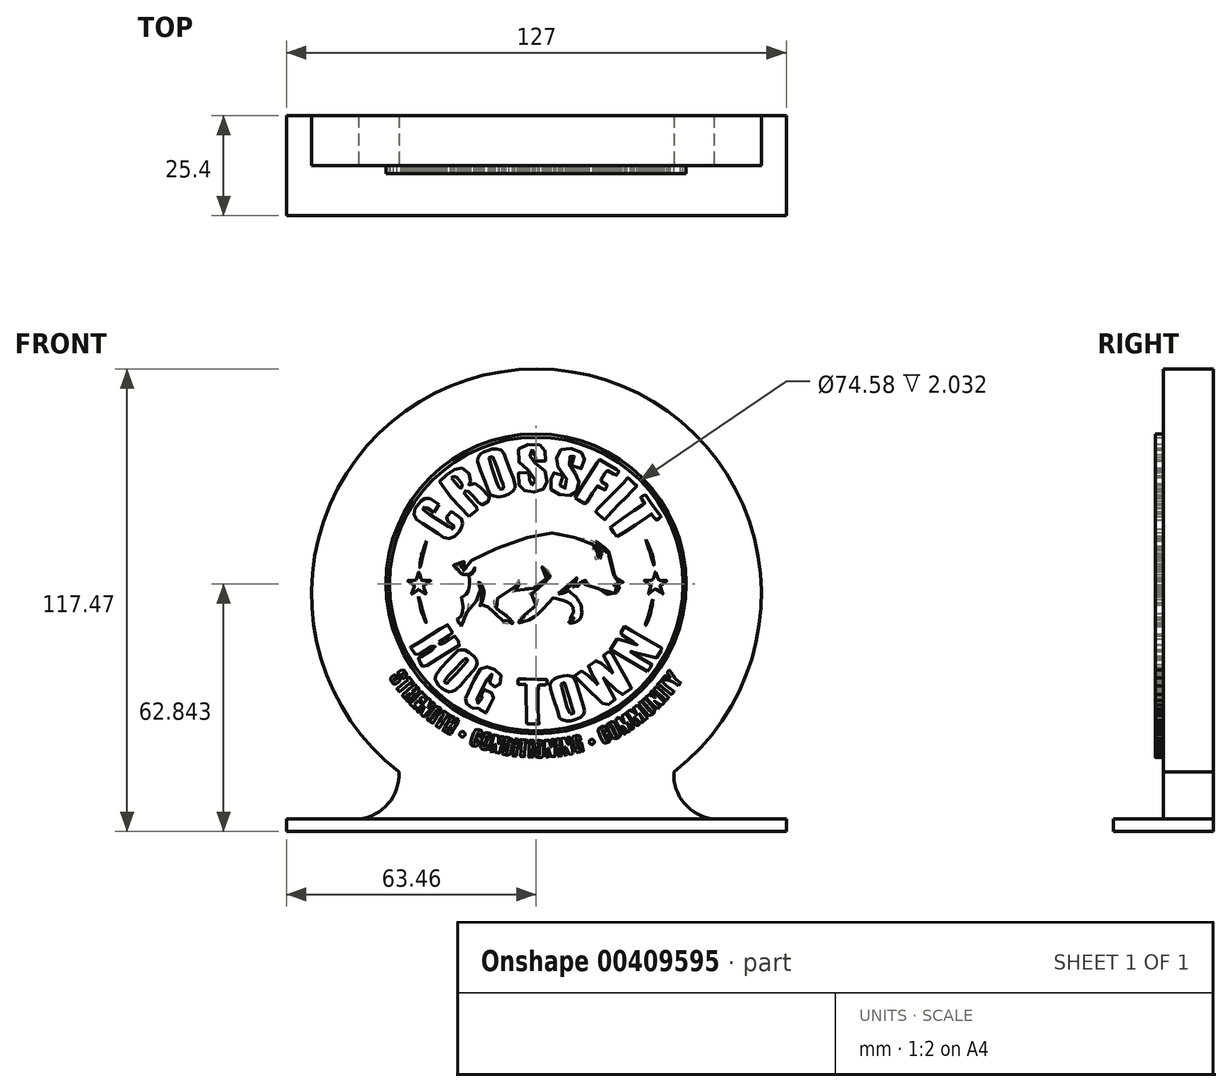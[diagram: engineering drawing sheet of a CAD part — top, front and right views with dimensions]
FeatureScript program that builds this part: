
annotation { "Feature Type Name" : "Feature", "Feature Type Description" : "" }
export const myFeature = defineFeature(function(context is Context, id is Id, definition is map)
    precondition{}
    {
        {
            var Q0;
            Q0=qCreatedBy(makeId("Front.planeOp"),FACE);
            var sketch = newSketch(context, id + "F0", { "sketchPlane" : qUnion([Q0])});
            skCircle(sketch, "E0", {"center": v(0, 0) * mm, "radius": 57.15 * mm});
            skSolve(sketch);
        }
        {
            var Q0;
            Q0=makeQuery(id+"F0.imprint","IMPRINT",FACE,{"disambiguationData":[TD([[makeQuery(id+"F0.imprint","IMPRINT",EDGE,{"derivedFrom":sQuery(id+"F0.wireOp",EDGE,"E0")}),1.0]])]});
            var Q1;
            Q1 = qSketchRegion(id + "F2", true);
            extrude(context, id + "F1", {"entities" : qUnion([Q0, Q1]), "endBound" : BoundingType.SYMMETRIC, "depth" : 12.7 * mm});
        }
        {
            var Q0;
            Q0=makeQuery(id+"F1.opExtrude","CAP_FACE",FACE,{"disambiguationData":[OSD([sQuery(id+"F0.wireOp",EDGE,"E0")])],"isStart":false});
            var sketch = newSketch(context, id + "F2", { "sketchPlane" : qUnion([Q0])});
            skLineSegment(sketch, "E1", {"start": v(-26.03, 20.73) * mm, "end": v(-24.68, 22.7) * mm});
            skLineSegment(sketch, "E2", {"start": v(-24.68, 22.7) * mm, "end": v(-27.02, 24.31) * mm});
            skLineSegment(sketch, "E3", {"start": v(-27.02, 24.31) * mm, "end": v(-28.26, 24.31) * mm});
            skLineSegment(sketch, "E4", {"start": v(-28.26, 24.31) * mm, "end": v(-29.26, 23.65) * mm});
            skLineSegment(sketch, "E5", {"start": v(-29.26, 23.65) * mm, "end": v(-29.82, 23.04) * mm});
            skLineSegment(sketch, "E6", {"start": v(-29.82, 23.04) * mm, "end": v(-30.8, 21.71) * mm});
            skFitSpline(sketch, "E7", {"points": [v(-30.8, 21.71) * mm, v(-31.11, 20.6) * mm, v(-31.07, 19.96) * mm, v(-30.75, 19.24) * mm, v(-30.26, 18.75) * mm, v(-29.9, 18.5) * mm, v(-24.5, 14.96) * mm, v(-23.85, 14.52) * mm, v(-23.25, 14.23) * mm, v(-22.46, 14.07) * mm, v(-21.58, 14.18) * mm, v(-20.96, 14.47) * mm, v(-20.27, 15.06) * mm, v(-19.58, 15.87) * mm, v(-19.22, 16.41) * mm, v(-18.95, 17.02) * mm, v(-18.83, 17.29) * mm, v(-18.77, 17.77) * mm, v(-18.77, 18.45) * mm, v(-18.92, 18.92) * mm, v(-19.05, 19.17) * mm, v(-19.78, 19.71) * mm, v(-20.83, 20.45) * mm, v(-21.65, 20.95) * mm, v(-21.9, 20.69) * mm, v(-23.14, 18.9) * mm, v(-22.76, 18.6) * mm, v(-21.87, 17.96) * mm, v(-21, 17.4) * mm, v(-20.84, 17.2) * mm, v(-20.9, 16.86) * mm, v(-21.1, 16.67) * mm, v(-21.37, 16.53) * mm, v(-21.6, 16.62) * mm, v(-28.58, 21.2) * mm, v(-28.7, 21.34) * mm, v(-28.76, 21.43) * mm, v(-28.83, 21.62) * mm, v(-28.76, 21.71) * mm, v(-28.66, 21.93) * mm, v(-28.58, 21.99) * mm, v(-28.44, 22) * mm, v(-28.3, 22) * mm, v(-27.91, 21.9) * mm, v(-27.7, 21.71) * mm, v(-26.03, 20.73) * mm], "startDerivative": vector(-13.88, -41.1) * mm, "endDerivative": vector(57.16, -30.64) * mm});
            skFitSpline(sketch, "E8", {"points": [v(-20.96, 7.43) * mm, v(-20.84, 7.32) * mm, v(-20.7, 7.19) * mm, v(-20.52, 7.06) * mm, v(-20.33, 6.94) * mm, v(-20.22, 6.9) * mm, v(-19.96, 6.93) * mm, v(-19.84, 7.17) * mm, v(-19.7, 7.51) * mm, v(-19.63, 7.75) * mm, v(-19.42, 8) * mm, v(-19.16, 8.16) * mm, v(-18.86, 8.24) * mm, v(-18.45, 8.24) * mm, v(-18.06, 8.21) * mm, v(-17.91, 8.1) * mm, v(-17.82, 7.92) * mm, v(-17.74, 7.68) * mm, v(-17.72, 7.12) * mm, v(-17.84, 6.7) * mm, v(-18.02, 6.44) * mm, v(-18.23, 6.24) * mm, v(-18.44, 6.16) * mm, v(-18.62, 6.16) * mm, v(-18.7, 6.16) * mm, v(-18.7, 6.09) * mm, v(-18.68, 6.04) * mm, v(-18.59, 6) * mm, v(-18.5, 5.96) * mm, v(-18.38, 5.94) * mm, v(-18.25, 5.96) * mm, v(-18.14, 5.98) * mm, v(-17.9, 6.14) * mm, v(-17.72, 6.39) * mm, v(-17.57, 6.73) * mm, v(-17.5, 7) * mm, v(-17.4, 7.27) * mm, v(-17.36, 7.4) * mm, v(-17.3, 7.6) * mm, v(-17.2, 7.81) * mm, v(-17.04, 8.03) * mm, v(-16.78, 8.3) * mm, v(-16.53, 8.54) * mm, v(-16.2, 8.76) * mm, v(-15.93, 8.94) * mm, v(-15.42, 9.25) * mm, v(-14.8, 9.61) * mm, v(-13.93, 10.01) * mm, v(-12.46, 10.62) * mm, v(-10.58, 11.38) * mm, v(-8.75, 12.19) * mm, v(-7.27, 12.8) * mm, v(-5.37, 13.5) * mm, v(-4.46, 13.8) * mm, v(-3.4, 14.1) * mm, v(-2.15, 14.33) * mm, v(-1.23, 14.55) * mm, v(-0.4, 14.75) * mm, v(0.32, 14.93) * mm, v(1.03, 15.1) * mm, v(1.85, 15.26) * mm, v(2.93, 15.46) * mm, v(4, 15.49) * mm, v(4.9, 15.5) * mm, v(5.62, 15.46) * mm, v(6.28, 15.34) * mm, v(6.85, 15.2) * mm, v(7.56, 14.98) * mm, v(7.94, 14.8) * mm, v(8.73, 14.53) * mm, v(9.67, 14.38) * mm, v(10.61, 14.33) * mm, v(11.59, 14.25) * mm, v(12.53, 14.12) * mm, v(13.25, 14.02) * mm, v(13.81, 13.82) * mm, v(14.52, 13.41) * mm, v(14.42, 13.15) * mm, v(14.36, 12.7) * mm, v(14.24, 12.16) * mm, v(14.3, 10.72) * mm, v(14.59, 8.86) * mm, v(14.82, 8.78) * mm, v(15.4, 8.76) * mm, v(16.12, 8.84) * mm, v(16.45, 8.9) * mm, v(16.47, 9) * mm, v(16.4, 9.06) * mm, v(16.2, 9.12) * mm, v(15.23, 9.12) * mm, v(15.13, 9.14) * mm, v(14.97, 9.22) * mm, v(14.69, 11.5) * mm, v(14.75, 12.07) * mm, v(14.8, 12.44) * mm, v(14.92, 12.88) * mm, v(15.15, 13.13) * mm, v(15.2, 13.38) * mm, v(15.46, 13.05) * mm, v(15.76, 12.62) * mm, v(15.9, 12.32) * mm, v(16.18, 11.9) * mm, v(16.29, 11.74) * mm, v(16.46, 11.58) * mm, v(16.62, 11.43) * mm, v(16.82, 11.27) * mm, v(16.98, 11.2) * mm, v(17.11, 11.2) * mm, v(17.27, 11.3) * mm, v(17.36, 11.4) * mm, v(17.4, 11.55) * mm, v(17.42, 11.65) * mm, v(17.5, 11.68) * mm, v(17.57, 11.59) * mm, v(17.7, 11.43) * mm, v(17.7, 11.27) * mm, v(17.68, 11.03) * mm, v(17.64, 10.85) * mm, v(17.59, 10.72) * mm, v(17.58, 10.54) * mm, v(17.58, 10.43) * mm, v(17.7, 10.3) * mm, v(17.79, 10.3) * mm, v(17.92, 10.35) * mm, v(18.04, 10.5) * mm, v(18.12, 10.67) * mm, v(18.14, 10.84) * mm, v(18.15, 10.9) * mm, v(18.22, 10.86) * mm, v(18.28, 10.77) * mm, v(18.34, 10.71) * mm, v(18.36, 10.56) * mm, v(18.4, 10.38) * mm, v(18.37, 10.26) * mm, v(18.34, 10.09) * mm, v(18.25, 9.83) * mm, v(18.2, 9.69) * mm, v(18.15, 9.57) * mm, v(18.17, 9.41) * mm, v(18.21, 9.39) * mm, v(18.32, 9.45) * mm, v(18.42, 9.6) * mm, v(18.53, 9.73) * mm, v(18.61, 9.84) * mm, v(18.66, 9.9) * mm, v(18.72, 9.9) * mm, v(18.76, 9.89) * mm, v(18.75, 9.7) * mm, v(18.69, 9.57) * mm, v(18.66, 9.4) * mm, v(18.66, 8.96) * mm, v(18.66, 8.37) * mm, v(18.75, 7.77) * mm, v(18.87, 7.16) * mm, v(19.12, 6.42) * mm, v(19.42, 5.56) * mm, v(19.82, 4.6) * mm, v(20.08, 3.83) * mm, v(20.11, 3.52) * mm, v(20.17, 3.36) * mm, v(20.2, 3.15) * mm, v(20.32, 3.1) * mm, v(20.67, 3.05) * mm, v(21.01, 3.07) * mm, v(21.4, 3.11) * mm, v(21.7, 3.14) * mm, v(21.93, 3.26) * mm, v(22.12, 3.3) * mm, v(22.22, 3.36) * mm, v(22.28, 3.35) * mm, v(22.05, 3.05) * mm, v(21.84, 2.9) * mm, v(21.4, 2.6) * mm, v(21.03, 2.49) * mm, v(20.78, 2.4) * mm, v(20.44, 2.31) * mm, v(20.19, 2.27) * mm, v(19.9, 2.27) * mm, v(19.77, 2.2) * mm, v(19.6, 2.24) * mm, v(19.52, 2.16) * mm, v(19.6, 1.99) * mm, v(19.87, 1.94) * mm, v(20.17, 1.96) * mm, v(20.48, 2) * mm, v(20.64, 2.03) * mm, v(20.8, 2.03) * mm, v(20.92, 1.94) * mm, v(21.06, 1.78) * mm, v(21.2, 1.54) * mm, v(21.28, 1.38) * mm, v(21.5, 1.25) * mm, v(21.57, 1.23) * mm, v(21.48, 0.97) * mm, v(21.18, 0.9) * mm, v(20.74, 0.55) * mm, v(20.37, 0.34) * mm, v(19.91, 0) * mm, v(18.53, -0.89) * mm, v(18.4, -0.7) * mm, v(18.25, -0.48) * mm, v(18.12, -0.23) * mm, v(17.97, -0.14) * mm, v(17.89, 0) * mm, v(17.78, 0.14) * mm, v(17.65, 0.29) * mm, v(17.34, 0.5) * mm, v(16.55, 1.05) * mm, v(16.28, 1.18) * mm, v(15.74, 1.41) * mm, v(15.17, 1.62) * mm, v(14.68, 1.82) * mm, v(14.32, 1.9) * mm, v(14.1, 2) * mm, v(13.57, 2.13) * mm, v(13.23, 2.2) * mm, v(12.85, 2.28) * mm, v(12.6, 2.3) * mm, v(12.48, 2.36) * mm, v(12.41, 2.4) * mm, v(12.28, 2.52) * mm, v(12.28, 2.68) * mm, v(12.26, 2.95) * mm, v(12.26, 3.1) * mm, v(12.35, 3.37) * mm, v(12.38, 3.53) * mm, v(12.46, 3.83) * mm, v(12.5, 3.96) * mm, v(12.54, 4.07) * mm, v(12.56, 4.12) * mm, v(12.35, 4.04) * mm, v(12.09, 3.84) * mm, v(11.92, 3.66) * mm, v(11.7, 3.35) * mm, v(11.58, 3.08) * mm, v(11.48, 2.67) * mm, v(11.45, 2.36) * mm, v(11.45, 2.06) * mm, v(11.43, 1.97) * mm, v(11.27, 1.92) * mm, v(10.8, 1.98) * mm, v(10.49, 1.92) * mm, v(10.28, 1.89) * mm, v(10, 1.82) * mm, v(9.74, 1.69) * mm, v(9.57, 1.64) * mm, v(9.33, 1.5) * mm, v(9.28, 1.53) * mm, v(9.4, 1.85) * mm, v(9.54, 2.13) * mm, v(9.69, 2.37) * mm, v(9.93, 2.72) * mm, v(10.01, 3.01) * mm, v(10.11, 3.17) * mm, v(10.18, 3.35) * mm, v(10.23, 3.61) * mm, v(10.26, 3.8) * mm, v(10.26, 4) * mm, v(10.28, 4.09) * mm, v(10.28, 4.2) * mm, v(10.24, 4.23) * mm, v(10.1, 4.07) * mm, v(9.97, 3.87) * mm, v(9.85, 3.63) * mm, v(9.6, 3.17) * mm, v(9.09, 2.6) * mm, v(8.34, 1.87) * mm, v(7.55, 1.27) * mm, v(6.43, 0.56) * mm, v(5.78, 0.25) * mm, v(5.63, 0.17) * mm, v(5.6, 0.16) * mm, v(5.6, 0) * mm], "startDerivative": vector(47.31, -39.9) * mm, "endDerivative": vector(8.08, -79.4) * mm});
            skFitSpline(sketch, "E9", {"points": [v(5.6, 0.07) * mm, v(6.07, 0.07) * mm, v(6.58, 0.17) * mm, v(6.84, 0.25) * mm, v(7.13, 0.36) * mm, v(7.66, 0.55) * mm, v(8.17, 0.9) * mm, v(8.23, 0.85) * mm, v(8.32, 0.76) * mm], "startDerivative": vector(3.12, -0.16) * mm, "endDerivative": vector(1.2, -1.25) * mm});
            skFitSpline(sketch, "E10", {"points": [v(8.32, 0.76) * mm, v(9.13, 0) * mm, v(10.05, -0.83) * mm, v(10.55, -1.34) * mm, v(10.85, -2) * mm, v(11.25, -2.54) * mm, v(11.45, -3.36) * mm, v(11.53, -4.1) * mm, v(11.53, -5.05) * mm, v(11.34, -5.7) * mm, v(11.12, -6.25) * mm, v(10.74, -6.69) * mm, v(10.33, -6.99) * mm, v(9.67, -7.26) * mm, v(9, -7.4) * mm, v(8.53, -7.4) * mm, v(8.32, -7.37) * mm, v(8.32, -7.31) * mm, v(8.32, -7.04) * mm, v(8.72, -6.88) * mm, v(9.05, -6.63) * mm, v(9.35, -6.47) * mm, v(9.37, -6.39) * mm], "startDerivative": vector(12.06, -11.32) * mm, "endDerivative": vector(0.2, 4.65) * mm});
            skFitSpline(sketch, "E11", {"points": [v(9.37, -6.39) * mm, v(9.47, -6.26) * mm, v(9.53, -6.15) * mm, v(9.57, -6.07) * mm, v(9.57, -6.05) * mm, v(9.46, -6.02) * mm, v(9.37, -6.02) * mm, v(9.23, -6.07) * mm, v(9.1, -6.13) * mm, v(9.01, -6.16) * mm, v(8.91, -6.23) * mm, v(8.78, -6.32) * mm, v(8.68, -6.39) * mm, v(8.58, -6.43) * mm, v(8.56, -6.3) * mm, v(8.67, -6.15) * mm, v(8.74, -6) * mm, v(8.78, -5.89) * mm, v(9.06, -5.28) * mm, v(9.37, -4.88) * mm, v(9.37, -4.35) * mm, v(9.37, -3.54) * mm, v(9, -2.9) * mm, v(8.66, -2.56) * mm, v(8.21, -2.25) * mm, v(7.6, -1.95) * mm, v(7.1, -1.78) * mm, v(6.44, -1.56) * mm, v(5.9, -1.4) * mm, v(5.4, -1.17) * mm, v(4.99, -1.07) * mm, v(4.6, -0.77) * mm, v(4.04, -1.24) * mm, v(2.73, -2.68) * mm, v(0.99, -4.58) * mm, v(0.16, -5.33) * mm, v(-0.86, -6.03) * mm, v(-1.85, -6.6) * mm, v(-2.73, -6.9) * mm, v(-3.71, -7.17) * mm, v(-4.52, -7.3) * mm, v(-4.52, -7.15) * mm, v(-4.48, -7.03) * mm, v(-4.37, -6.83) * mm, v(-4.1, -6.56) * mm, v(-3.85, -6.39) * mm, v(-3.6, -6.3) * mm, v(-3.5, -6.29) * mm, v(-3.46, -6.24) * mm, v(-3.46, -6.16) * mm, v(-3.47, -6.14) * mm], "startDerivative": vector(7.74, 9.79) * mm, "endDerivative": vector(-1.21, 3.19) * mm});
            skFitSpline(sketch, "E12", {"points": [v(-3.46, -6.16) * mm, v(-3.62, -6.16) * mm, v(-3.88, -6.16) * mm, v(-3.93, -6.16) * mm, v(-4.06, -6.11) * mm, v(-4.05, -6.03) * mm, v(-4, -5.93) * mm, v(-3.93, -5.78) * mm, v(-3.78, -5.63) * mm, v(-3.4, -5.38) * mm, v(-2.95, -5.27) * mm, v(-2.55, -5.2) * mm, v(-2.3, -5.13) * mm, v(-2, -5.12) * mm, v(-1.33, -4.54) * mm, v(-0.25, -3.18) * mm, v(0.43, -1.6) * mm, v(0.64, -0.43) * mm, v(0.3, 0) * mm, v(-0.65, 0) * mm, v(-2.08, 0) * mm, v(-1.21, 0.5) * mm, v(-0.74, 0.79) * mm, v(-0.25, 1.04) * mm, v(0.22, 1.28) * mm, v(0.69, 1.65) * mm, v(1.42, 2.1) * mm, v(2.57, 3.04) * mm, v(3.46, 4.07) * mm, v(3.46, 4.54) * mm, v(3.48, 4.94) * mm, v(3.25, 5.48) * mm, v(2.68, 6.2) * mm, v(1.8, 6.82) * mm, v(1.44, 6.86) * mm, v(1.89, 6.25) * mm, v(2.36, 5.71) * mm, v(2.59, 5.38) * mm, v(2.7, 4.92) * mm, v(2.68, 4.28) * mm, v(2.4, 3.72) * mm, v(1.8, 3.2) * mm, v(0.31, 2.17) * mm, v(-0.65, 1.47) * mm, v(-0.72, 1.42) * mm, v(-1.02, 1.5) * mm, v(-1.7, 1.65) * mm, v(-2.74, 1.6) * mm, v(-4.21, 1.23) * mm, v(-5.43, 0.7) * mm, v(-5.9, 0.43) * mm, v(-5.9, 0.72) * mm, v(-5.43, 1.16) * mm, v(-4.87, 1.87) * mm, v(-4.45, 2.5) * mm, v(-4.3, 3.1) * mm, v(-4.38, 3.67) * mm, v(-4.7, 3.23) * mm, v(-5.08, 2.6) * mm, v(-5.88, 1.6) * mm, v(-6.82, 0.8) * mm, v(-7.5, 0.32) * mm, v(-8.48, -0.39) * mm, v(-9.87, -1.11) * mm, v(-10.76, -1.72) * mm, v(-10.92, -1.82) * mm, v(-10.9, -2.31) * mm, v(-10.69, -2.83) * mm, v(-10.45, -3.23) * mm, v(-9.94, -3.76) * mm, v(-9.37, -4.3) * mm, v(-8.46, -4.91) * mm, v(-7.69, -5.4) * mm, v(-6.94, -6.16) * mm, v(-6.42, -6.72) * mm, v(-5.95, -7.42) * mm, v(-6.35, -7.52) * mm, v(-6.54, -7.33) * mm, v(-6.68, -7.1) * mm, v(-6.82, -6.86) * mm, v(-6.98, -6.67) * mm, v(-7.03, -6.86) * mm, v(-7.05, -7.12) * mm, v(-7.05, -7.42) * mm, v(-7.05, -7.54) * mm, v(-8.2, -7.5) * mm, v(-8.41, -7.42) * mm, v(-8.53, -6.77) * mm, v(-8.74, -6.16) * mm, v(-9.75, -5.31) * mm, v(-11.42, -3.9) * mm, v(-12.78, -3.13) * mm, v(-13.15, -3.01) * mm, v(-13.48, -2.97) * mm, v(-13.79, -2.97) * mm, v(-14.04, -2.97) * mm, v(-14.25, -2.97) * mm, v(-14.4, -2.97) * mm, v(-14.18, -2.7) * mm, v(-13.67, -1.56) * mm, v(-13.34, 0) * mm, v(-13.43, 1) * mm, v(-13.62, 1.72) * mm, v(-14, 2.43) * mm, v(-14.3, 2.76) * mm, v(-14.68, 3) * mm, v(-14.58, 2.43) * mm, v(-14.37, 1.75) * mm, v(-14.18, 0.65) * mm, v(-14.14, 0) * mm, v(-14.2, -0.72) * mm, v(-14.3, -1.42) * mm, v(-14.98, -1.77) * mm, v(-15.85, -2.1) * mm, v(-16.65, -2.36) * mm, v(-17.14, -2.36) * mm, v(-17.35, -3.06) * mm, v(-17.63, -4.52) * mm, v(-18.08, -6.42) * mm, v(-18.57, -7.45) * mm, v(-18.92, -7.92) * mm, v(-19.11, -8.08) * mm, v(-19.18, -8.2) * mm, v(-19.2, -8.22) * mm], "startDerivative": vector(-33.94, -0.17) * mm, "endDerivative": vector(-12.22, -9.19) * mm});
            skFitSpline(sketch, "E13", {"points": [v(-20.96, 7.43) * mm, v(-21.02, 7.34) * mm, v(-20.94, 7.08) * mm, v(-20.68, 6.8) * mm], "startDerivative": vector(-0.38, -0.3) * mm, "endDerivative": vector(0.68, -0.6) * mm});
            skFitSpline(sketch, "E14", {"points": [v(-20.68, 6.8) * mm, v(-20.26, 6.38) * mm, v(-19.84, 6.15) * mm, v(-19.8, 6.04) * mm, v(-19.52, 5.54) * mm, v(-19.04, 5.13) * mm, v(-18.45, 4.94) * mm, v(-17.7, 4.93) * mm, v(-17.07, 5.07) * mm, v(-16.58, 5.39) * mm, v(-16, 5.94) * mm, v(-15.86, 6.2) * mm, v(-15.7, 6.56) * mm, v(-15.65, 6.67) * mm, v(-15.6, 6.5) * mm, v(-15.64, 6.04) * mm, v(-15.82, 5.55) * mm, v(-16.2, 5.11) * mm, v(-16.6, 4.82) * mm, v(-16.86, 4.63) * mm, v(-17.2, 4.43) * mm, v(-17.15, 4.14) * mm, v(-16.99, 3.4) * mm, v(-16.94, 2.82) * mm, v(-17, 1.85) * mm, v(-17.23, 0.9) * mm, v(-17.55, 0.3) * mm, v(-18.02, -0.3) * mm, v(-18.9, -0.87) * mm, v(-19.29, -0.94) * mm, v(-19.08, -1.37) * mm, v(-18.75, -2.36) * mm, v(-18.62, -3.5) * mm, v(-18.68, -4.35) * mm, v(-18.83, -5.04) * mm, v(-19.16, -5.6) * mm, v(-19.68, -6.12) * mm, v(-20.07, -6.3) * mm, v(-20.02, -6.7) * mm, v(-19.73, -7.4) * mm, v(-19.56, -7.65) * mm, v(-19.4, -7.68) * mm, v(-19.25, -7.56) * mm, v(-19.16, -7.48) * mm, v(-19.05, -7.57) * mm, v(-19.06, -7.73) * mm, v(-19.16, -7.9) * mm, v(-19.25, -8.1) * mm, v(-19.29, -8.2) * mm, v(-19.27, -8.25) * mm, v(-19.23, -8.25) * mm, v(-19.2, -8.22) * mm], "startDerivative": vector(15.97, -20.26) * mm, "endDerivative": vector(2.66, 6.78) * mm});
            skFitSpline(sketch, "E15", {"points": [v(-18.8, 7.66) * mm, v(-19, 7.52) * mm, v(-19.16, 7.15) * mm, v(-19.16, 6.8) * mm, v(-18.91, 6.72) * mm, v(-18.62, 6.8) * mm, v(-18.47, 6.9) * mm, v(-18.4, 7.08) * mm, v(-18.34, 7.35) * mm, v(-18.36, 7.43) * mm, v(-18.41, 7.59) * mm, v(-18.58, 7.68) * mm, v(-18.8, 7.66) * mm]});
            skFitSpline(sketch, "E16", {"points": [v(15.4, 12.2) * mm, v(16.1, 11.52) * mm, v(16.47, 10.8) * mm, v(16.6, 10.31) * mm, v(16.57, 10.04) * mm, v(16.26, 9.68) * mm, v(15.9, 9.52) * mm, v(15.64, 9.47) * mm, v(15.61, 9.68) * mm, v(15.45, 10.44) * mm, v(15.25, 11.07) * mm, v(15.23, 11.58) * mm, v(15.21, 11.84) * mm, v(15.4, 12.2) * mm]});
            skFitSpline(sketch, "E17", {"points": [v(-17.06, 19.67) * mm, v(-24.64, 28.47) * mm, v(-24.57, 28.54) * mm, v(-23.96, 29.13) * mm, v(-22.2, 30.82) * mm, v(-20.96, 31.58) * mm, v(-19.46, 32) * mm, v(-18.75, 31.93) * mm, v(-18.24, 31.7) * mm, v(-16.74, 29.92) * mm, v(-16.63, 29.2) * mm, v(-17.15, 27.98) * mm, v(-17.45, 27.56) * mm, v(-16.88, 27.86) * mm, v(-16.24, 28.02) * mm, v(-15.53, 28.02) * mm, v(-14.86, 27.73) * mm, v(-14.17, 27.07) * mm, v(-11.98, 24.65) * mm, v(-11.33, 24.27) * mm, v(-11.36, 24.15) * mm, v(-13.46, 22.6) * mm, v(-13.55, 22.55) * mm, v(-13.73, 22.58) * mm, v(-13.9, 22.64) * mm, v(-14.07, 22.7) * mm, v(-14.23, 22.84) * mm, v(-15, 23.58) * mm, v(-15.54, 24.15) * mm, v(-16.3, 25.07) * mm, v(-17, 25.77) * mm, v(-17.26, 26.05) * mm, v(-17.57, 26.18) * mm, v(-17.76, 26.18) * mm, v(-17.9, 26.2) * mm, v(-18, 26.2) * mm, v(-18.05, 26.16) * mm, v(-18.23, 26.06) * mm, v(-18.35, 25.96) * mm, v(-18.47, 25.9) * mm, v(-18.25, 25.53) * mm, v(-17.48, 24.64) * mm, v(-15.85, 22.73) * mm, v(-15.16, 22.01) * mm, v(-15.03, 21.83) * mm, v(-14.74, 21.55) * mm, v(-15.04, 21.3) * mm, v(-15.56, 20.91) * mm, v(-16.14, 20.5) * mm, v(-16.5, 20.13) * mm, v(-16.83, 19.9) * mm, v(-16.94, 19.78) * mm, v(-17.06, 19.67) * mm]});
            skFitSpline(sketch, "E18", {"points": [v(-21.5, 29.47) * mm, v(-21, 29.78) * mm, v(-20.4, 29.73) * mm, v(-19.9, 29.25) * mm, v(-19.4, 28.66) * mm, v(-18.95, 28.06) * mm, v(-18.89, 27.31) * mm, v(-19.2, 26.87) * mm, v(-19.46, 27.03) * mm, v(-19.85, 27.42) * mm, v(-20.25, 27.84) * mm, v(-20.67, 28.33) * mm, v(-20.89, 28.63) * mm, v(-21.1, 28.9) * mm, v(-21.29, 29.2) * mm, v(-21.5, 29.47) * mm]});
            skFitSpline(sketch, "E19", {"points": [v(-11.98, 25.8) * mm, v(-14.85, 33.18) * mm, v(-14.97, 34.42) * mm, v(-14.37, 35.35) * mm, v(-13.63, 36) * mm, v(-12.58, 36.42) * mm, v(-11.44, 36.76) * mm, v(-10.24, 36.88) * mm, v(-9.17, 36.64) * mm, v(-8.26, 35.66) * mm, v(-7.67, 34.1) * mm, v(-5.42, 28.07) * mm, v(-5.4, 27.47) * mm, v(-5.5, 26.8) * mm, v(-6.04, 26.06) * mm, v(-7.38, 25.25) * mm, v(-8.98, 24.65) * mm, v(-10.58, 24.85) * mm, v(-11.15, 24.99) * mm, v(-11.72, 25.35) * mm, v(-11.98, 25.8) * mm]});
            skFitSpline(sketch, "E20", {"points": [v(-9.34, 26.85) * mm, v(-11.98, 34.28) * mm, v(-11.98, 34.63) * mm, v(-11.53, 34.8) * mm, v(-11.03, 34.68) * mm, v(-10.89, 34.4) * mm, v(-8.31, 27.16) * mm, v(-8.36, 26.97) * mm, v(-8.57, 26.76) * mm, v(-8.98, 26.7) * mm, v(-9.34, 26.85) * mm]});
            skFitSpline(sketch, "E21", {"points": [v(-1.82, 30.81) * mm, v(-4.5, 30.81) * mm, v(-4.5, 30.72) * mm, v(-4.42, 27.88) * mm, v(-4, 26.9) * mm, v(-3.01, 26.2) * mm, v(-1.46, 25.9) * mm, v(0.52, 26.09) * mm, v(2, 26.76) * mm, v(2.53, 27.57) * mm, v(2.7, 30.1) * mm, v(1.88, 31.48) * mm, v(-0.48, 33.37) * mm, v(-1.39, 34.37) * mm, v(-1.65, 35.56) * mm, v(-1.48, 36.52) * mm, v(-0.72, 36.33) * mm, v(-0.43, 35.73) * mm, v(-0.41, 35.3) * mm, v(-0.36, 33.77) * mm, v(-0.24, 33.82) * mm, v(0.23, 33.8) * mm, v(2.29, 33.82) * mm, v(2.29, 34.13) * mm, v(2.2, 36.64) * mm, v(1.71, 37.43) * mm, v(0, 38.02) * mm, v(-2.7, 37.88) * mm, v(-4.35, 37.04) * mm, v(-4.61, 33.96) * mm, v(-3.23, 32.25) * mm, v(-0.67, 30.22) * mm, v(-0.36, 28.02) * mm, v(-0.6, 27.83) * mm, v(-1.1, 27.69) * mm, v(-1.68, 28.02) * mm, v(-1.75, 28.5) * mm, v(-1.77, 30.43) * mm, v(-1.8, 30.58) * mm, v(-1.82, 30.81) * mm]});
            skFitSpline(sketch, "E22", {"points": [v(8.98, 32.58) * mm, v(9.55, 34.58) * mm, v(9.48, 35.13) * mm, v(8.89, 35.38) * mm, v(8.47, 34.87) * mm, v(8.13, 33.7) * mm, v(8.77, 32.15) * mm, v(9.83, 30.57) * mm, v(10.7, 29.06) * mm, v(10.63, 27.36) * mm, v(9.97, 25.79) * mm, v(9.15, 25.19) * mm, v(7.93, 25) * mm, v(5.52, 25.35) * mm, v(3.94, 26.36) * mm, v(3.36, 27.24) * mm, v(3.96, 30.24) * mm, v(4.12, 30.8) * mm, v(4.94, 30.57) * mm, v(6.75, 30.1) * mm, v(6.81, 29.94) * mm, v(6, 27.48) * mm, v(6.46, 26.82) * mm, v(7.27, 26.88) * mm, v(7.71, 29.08) * mm, v(7.6, 29.28) * mm, v(5.3, 32.63) * mm, v(5.04, 33.69) * mm, v(5.6, 35.98) * mm, v(6.46, 36.82) * mm, v(8.31, 37.04) * mm, v(10.87, 36.34) * mm, v(11.9, 35.5) * mm, v(12.26, 34.63) * mm, v(11.58, 31.81) * mm, v(11.54, 31.77) * mm, v(9.27, 32.43) * mm, v(8.98, 32.58) * mm]});
            skFitSpline(sketch, "E23", {"points": [v(9.86, 24.44) * mm, v(15.95, 34.14) * mm, v(16.03, 34.18) * mm, v(20.96, 31.35) * mm, v(21.04, 31.28) * mm, v(20.4, 30.16) * mm, v(20.34, 30.08) * mm, v(18, 31.38) * mm, v(17.94, 31.41) * mm, v(16.26, 28.74) * mm, v(16.23, 28.69) * mm, v(18.03, 27.64) * mm, v(18.14, 27.57) * mm, v(17.56, 26.57) * mm, v(17.5, 26.44) * mm, v(15.63, 27.47) * mm, v(15.53, 27.52) * mm, v(12.56, 22.9) * mm, v(12.51, 22.84) * mm, v(10, 24.26) * mm, v(9.86, 24.44) * mm]});
            skFitSpline(sketch, "E24", {"points": [v(15.11, 21.06) * mm, v(23.11, 29.4) * mm, v(23.22, 29.54) * mm, v(25.42, 27.61) * mm, v(25.54, 27.55) * mm, v(17.47, 18.98) * mm, v(17.33, 18.87) * mm, v(15.16, 20.81) * mm, v(15.11, 21.06) * mm]});
            skFitSpline(sketch, "E25", {"points": [v(20.49, 14.55) * mm, v(18.77, 16.92) * mm, v(18.84, 16.98) * mm, v(27.36, 22.84) * mm, v(27.56, 22.95) * mm, v(26.48, 24.4) * mm, v(26.46, 24.49) * mm, v(27.47, 25.23) * mm, v(27.56, 25.3) * mm, v(31.6, 19.73) * mm, v(31.7, 19.55) * mm, v(30.53, 18.8) * mm, v(30.47, 18.79) * mm, v(29.34, 20.25) * mm, v(29.27, 20.34) * mm, v(20.85, 14.75) * mm, v(20.71, 14.75) * mm, v(20.49, 14.55) * mm]});
            skFitSpline(sketch, "E26", {"points": [v(-24.7, -12.21) * mm, v(-21.16, -9.98) * mm, v(-21.16, -9.93) * mm, v(-22.56, -7.82) * mm, v(-22.61, -7.75) * mm, v(-31.92, -13.54) * mm, v(-31.97, -13.58) * mm, v(-30.56, -15.75) * mm, v(-30.5, -15.8) * mm, v(-26.07, -13.02) * mm, v(-25.98, -13.06) * mm, v(-25.58, -13.6) * mm, v(-25.72, -13.71) * mm, v(-29.5, -16.13) * mm, v(-29.7, -16.13) * mm, v(-30.04, -16.34) * mm, v(-29.57, -17.36) * mm, v(-29.2, -17.86) * mm, v(-28.7, -18.67) * mm, v(-28.55, -18.6) * mm, v(-19.24, -12.9) * mm, v(-19.2, -12.83) * mm, v(-20.63, -10.73) * mm, v(-20.76, -10.7) * mm, v(-24.4, -12.94) * mm, v(-24.37, -12.82) * mm, v(-24.43, -12.82) * mm, v(-24.72, -12.38) * mm, v(-24.7, -12.21) * mm]});
            skFitSpline(sketch, "E27", {"points": [v(-25.56, -20.56) * mm, v(-20.39, -14.77) * mm, v(-19.76, -14.3) * mm, v(-18.53, -14.18) * mm, v(-16.63, -15.17) * mm, v(-15.2, -16.8) * mm, v(-15.14, -18.2) * mm, v(-15.74, -19.09) * mm, v(-20.49, -24.38) * mm, v(-21.52, -24.82) * mm, v(-22.55, -24.78) * mm, v(-23.86, -24.08) * mm, v(-25.03, -22.95) * mm, v(-25.64, -21.84) * mm, v(-25.56, -20.56) * mm]});
            skFitSpline(sketch, "E28", {"points": [v(-23.34, -22.12) * mm, v(-18.23, -16.49) * mm, v(-18.07, -16.38) * mm, v(-17.48, -16.8) * mm, v(-17.52, -17.03) * mm, v(-22.59, -22.64) * mm, v(-22.69, -22.7) * mm, v(-23.2, -22.48) * mm, v(-23.3, -22.32) * mm, v(-23.34, -22.12) * mm]});
            skFitSpline(sketch, "E29", {"points": [v(-18.03, -26.54) * mm, v(-14.47, -19.3) * mm, v(-14.2, -19) * mm, v(-13.5, -18.64) * mm, v(-12.47, -18.5) * mm, v(-11.77, -18.78) * mm, v(-9.54, -19.75) * mm, v(-8.87, -20.86) * mm, v(-8.72, -21.46) * mm, v(-9.75, -23.93) * mm, v(-9.85, -23.97) * mm, v(-11.96, -22.97) * mm, v(-12.07, -22.92) * mm, v(-11.11, -20.8) * mm, v(-11.27, -20.4) * mm, v(-11.78, -20.23) * mm, v(-11.84, -20.35) * mm, v(-15.27, -27.13) * mm, v(-15.27, -27.42) * mm, v(-15.18, -27.61) * mm, v(-14.68, -27.8) * mm, v(-14.35, -27.46) * mm, v(-13.55, -25.92) * mm, v(-13.6, -25.83) * mm, v(-14.07, -25.68) * mm, v(-13.9, -25.22) * mm, v(-13.45, -24.31) * mm, v(-13.24, -24.28) * mm, v(-11.86, -24.87) * mm, v(-10.54, -25.48) * mm, v(-10.6, -25.7) * mm, v(-12.86, -30.31) * mm, v(-12.97, -30.35) * mm, v(-14.1, -29.72) * mm, v(-14.07, -28.97) * mm, v(-14.35, -28.95) * mm, v(-14.62, -29.1) * mm, v(-15.64, -29.13) * mm, v(-16.56, -28.82) * mm, v(-17.55, -28.13) * mm, v(-17.96, -27.29) * mm, v(-18.03, -26.8) * mm, v(-18.03, -26.54) * mm]});
            skFitSpline(sketch, "E30", {"points": [v(-2.61, -23.03) * mm, v(-4.6, -23) * mm, v(-4.62, -22.93) * mm, v(-4.65, -21.68) * mm, v(-4.64, -21.6) * mm, v(2.59, -21.66) * mm, v(2.72, -21.66) * mm, v(2.72, -22.94) * mm, v(2.72, -23.08) * mm, v(0.7, -23.04) * mm, v(0.56, -23.03) * mm, v(0.65, -32.87) * mm, v(0.65, -33) * mm, v(-2.53, -32.95) * mm, v(-2.5, -32.9) * mm, v(-2.63, -23.21) * mm, v(-2.61, -23.03) * mm]});
            skFitSpline(sketch, "E31", {"points": [v(5.93, -31.5) * mm, v(3.57, -23.97) * mm, v(3.53, -22.82) * mm, v(4.28, -21.76) * mm, v(5.68, -21.12) * mm, v(7.06, -20.78) * mm, v(8.56, -20.82) * mm, v(9.6, -21.46) * mm, v(10.34, -23.42) * mm, v(12.1, -29.17) * mm, v(12.16, -29.58) * mm, v(12.1, -30.4) * mm, v(11.06, -31.42) * mm, v(9.1, -32.16) * mm, v(7.53, -32.23) * mm, v(6.06, -31.72) * mm, v(5.93, -31.5) * mm]});
            skFitSpline(sketch, "E32", {"points": [v(8.51, -30.37) * mm, v(6.32, -23.08) * mm, v(6.35, -22.86) * mm, v(6.57, -22.69) * mm, v(7.08, -22.64) * mm, v(7.26, -22.84) * mm, v(9.42, -30.1) * mm, v(9.4, -30.25) * mm, v(8.9, -30.42) * mm, v(8.68, -30.4) * mm, v(8.51, -30.37) * mm]});
            skFitSpline(sketch, "E33", {"points": [v(15.7, -23.14) * mm, v(11.82, -19.42) * mm, v(11.78, -19.4) * mm, v(9.7, -20.8) * mm, v(9.72, -20.95) * mm, v(17.61, -28.55) * mm, v(17.71, -28.56) * mm, v(20.04, -26.88) * mm, v(20.04, -26.86) * mm, v(16.9, -21.23) * mm, v(16.9, -21.17) * mm, v(21.64, -25.78) * mm, v(21.7, -25.76) * mm, v(24.12, -23.97) * mm, v(24.16, -23.97) * mm, v(18.77, -14.47) * mm, v(18.77, -14.54) * mm, v(18.57, -14.6) * mm, v(17.13, -15.62) * mm, v(17.11, -15.79) * mm, v(19.53, -20.25) * mm, v(19.49, -20.25) * mm, v(15.7, -16.81) * mm, v(15.59, -16.72) * mm, v(13.29, -18.26) * mm, v(13.19, -18.34) * mm, v(15.58, -22.96) * mm, v(15.7, -23.14) * mm]});
            skFitSpline(sketch, "E34", {"points": [v(28.28, -19.63) * mm, v(18.77, -14.08) * mm, v(18.77, -14.04) * mm, v(20.33, -11.57) * mm, v(20.41, -11.49) * mm, v(25.7, -12.92) * mm, v(25.75, -12.94) * mm, v(21.3, -10.2) * mm, v(21.23, -10.18) * mm, v(22.4, -8.38) * mm, v(22.47, -8.3) * mm, v(31.9, -13.76) * mm, v(32.05, -13.86) * mm, v(30.53, -16.24) * mm, v(30.47, -16.3) * mm, v(23.97, -14.6) * mm, v(23.86, -14.6) * mm, v(29.42, -17.9) * mm, v(29.47, -17.9) * mm, v(28.44, -19.52) * mm, v(28.28, -19.63) * mm]});
            skFitSpline(sketch, "E35", {"points": [v(-27.88, 13.48) * mm, v(-29.63, 6.67) * mm, v(-29.63, 6.68) * mm, v(-29.6, 7.7) * mm, v(-29.4, 8.7) * mm, v(-29.15, 10.05) * mm, v(-28.77, 11.16) * mm, v(-28.33, 12.5) * mm, v(-27.88, 13.48) * mm]});
            skFitSpline(sketch, "E36", {"points": [v(-29.94, -0.68) * mm, v(-28.86, -4.37) * mm, v(-28.01, -7.26) * mm, v(-28.12, -7.1) * mm, v(-28.9, -5.29) * mm, v(-29.57, -3.03) * mm, v(-29.94, -0.68) * mm]});
            skFitSpline(sketch, "E37", {"points": [v(27.84, 13.82) * mm, v(28.98, 10.12) * mm, v(29.88, 7.3) * mm, v(29.5, 9.67) * mm, v(28.82, 11.68) * mm, v(27.84, 13.82) * mm]});
            skFitSpline(sketch, "E38", {"points": [v(29.6, -1.39) * mm, v(28.58, -4.96) * mm, v(27.7, -8.02) * mm, v(28.74, -5.75) * mm, v(29.6, -1.39) * mm]});
            skFitSpline(sketch, "E39", {"points": [v(-30.57, 3.5) * mm, v(-29.94, 5.5) * mm, v(-29.9, 5.58) * mm, v(-29.83, 5.44) * mm, v(-29.16, 3.43) * mm, v(-29.16, 3.41) * mm, v(-26.92, 3.43) * mm, v(-26.83, 3.41) * mm, v(-28.64, 2.13) * mm, v(-28.74, 2.07) * mm, v(-28.03, 0) * mm, v(-28.01, -0.1) * mm, v(-29.83, 1.19) * mm, v(-29.88, 1.25) * mm, v(-31.6, 0) * mm, v(-31.68, 0) * mm, v(-31.02, 2) * mm, v(-31, 2.1) * mm, v(-32.81, 3.34) * mm, v(-32.86, 3.41) * mm, v(-30.84, 3.43) * mm, v(-30.57, 3.5) * mm]});
            skFitSpline(sketch, "E40", {"points": [v(29.6, 3.63) * mm, v(30.23, 5.47) * mm, v(30.27, 5.62) * mm, v(30.98, 3.59) * mm, v(31, 3.44) * mm, v(33.17, 3.51) * mm, v(33.25, 3.48) * mm, v(31.5, 2.2) * mm, v(31.43, 2.09) * mm, v(32.14, 0) * mm, v(32, 0.13) * mm, v(30.35, 1.36) * mm, v(30.3, 1.42) * mm, v(28.64, 0.15) * mm, v(28.5, 0) * mm, v(29.12, 2.07) * mm, v(29.15, 2.18) * mm, v(27.31, 3.44) * mm, v(27.25, 3.51) * mm, v(29.48, 3.5) * mm, v(29.6, 3.63) * mm]});
            skFitSpline(sketch, "E41", {"points": [v(-35.46, -21.15) * mm, v(-35.93, -20.48) * mm, v(-36, -20.5) * mm, v(-36.9, -21.18) * mm, v(-37, -21.36) * mm, v(-37.03, -21.74) * mm, v(-36.92, -22.08) * mm, v(-36.57, -22.63) * mm, v(-36.16, -22.93) * mm, v(-35.62, -22.84) * mm, v(-34.85, -22.3) * mm, v(-34.63, -21.74) * mm, v(-34.43, -20.63) * mm, v(-34.27, -20.42) * mm, v(-33.81, -20.12) * mm, v(-33.73, -20.2) * mm, v(-33.7, -20.36) * mm, v(-34.34, -20.8) * mm, v(-34.27, -20.96) * mm, v(-33.89, -21.55) * mm, v(-33.76, -21.48) * mm, v(-33.04, -20.97) * mm, v(-32.97, -20.28) * mm, v(-33.5, -19.5) * mm, v(-34.06, -19.29) * mm, v(-34.5, -19.45) * mm, v(-35.1, -19.9) * mm, v(-35.47, -21.6) * mm, v(-35.6, -21.72) * mm, v(-36.03, -22.03) * mm, v(-36.2, -22.02) * mm, v(-36.29, -21.85) * mm, v(-36.2, -21.7) * mm, v(-35.57, -21.25) * mm, v(-35.46, -21.15) * mm]});
            skFitSpline(sketch, "E42", {"points": [v(-32.58, -21.8) * mm, v(-32.81, -21.5) * mm, v(-32.84, -21.4) * mm, v(-32.48, -21.13) * mm, v(-32.42, -21.07) * mm, v(-31.22, -22.54) * mm, v(-31.17, -22.62) * mm, v(-31.58, -22.96) * mm, v(-31.65, -23) * mm, v(-31.91, -22.62) * mm, v(-31.96, -22.58) * mm, v(-34.8, -24.87) * mm, v(-34.85, -24.82) * mm, v(-35.4, -24.2) * mm, v(-35.42, -24.08) * mm, v(-32.65, -21.9) * mm, v(-32.58, -21.8) * mm]});
            skFitSpline(sketch, "E43", {"points": [v(-31.99, -25.14) * mm, v(-33.4, -26.43) * mm, v(-33.44, -26.5) * mm, v(-34.04, -25.84) * mm, v(-34.07, -25.75) * mm, v(-30.95, -22.93) * mm, v(-30.9, -22.94) * mm, v(-29.94, -24.06) * mm, v(-29.82, -24.47) * mm, v(-29.84, -24.82) * mm, v(-30.57, -25.5) * mm, v(-30.85, -25.55) * mm, v(-31.21, -25.44) * mm, v(-31.26, -25.42) * mm, v(-31.22, -25.6) * mm, v(-31.2, -26.07) * mm, v(-31.48, -26.31) * mm, v(-32.15, -26.92) * mm, v(-32.47, -27.23) * mm, v(-32.5, -27.5) * mm, v(-33.18, -26.8) * mm, v(-33.13, -26.6) * mm, v(-31.82, -25.4) * mm, v(-31.84, -25.17) * mm, v(-31.99, -25.14) * mm]});
            skFitSpline(sketch, "E44", {"points": [v(-31.57, -24.72) * mm, v(-30.74, -24) * mm, v(-30.7, -24.01) * mm, v(-30.6, -24.14) * mm, v(-30.71, -24.37) * mm, v(-31.23, -24.86) * mm, v(-31.43, -24.85) * mm, v(-31.57, -24.72) * mm]});
            skFitSpline(sketch, "E45", {"points": [v(-28.83, -26.05) * mm, v(-28.27, -26.54) * mm, v(-28.21, -26.55) * mm, v(-27.85, -26.19) * mm, v(-27.85, -26.15) * mm, v(-29.07, -24.93) * mm, v(-29.13, -24.89) * mm, v(-32.08, -27.84) * mm, v(-32.13, -27.93) * mm, v(-31.9, -28.17) * mm, v(-30.88, -29.17) * mm, v(-30.8, -29.2) * mm, v(-30.47, -28.86) * mm, v(-30.45, -28.8) * mm, v(-31.01, -28.2) * mm, v(-31.02, -28.1) * mm, v(-30.07, -27.18) * mm, v(-30.01, -27.17) * mm, v(-29.48, -27.7) * mm, v(-29.41, -27.66) * mm, v(-29.07, -27.34) * mm, v(-29.08, -27.26) * mm, v(-29.6, -26.79) * mm, v(-29.6, -26.67) * mm, v(-28.93, -26.05) * mm, v(-28.83, -26.05) * mm]});
            skFitSpline(sketch, "E46", {"points": [v(-29.78, -30.17) * mm, v(-30.38, -29.64) * mm, v(-30.3, -29.51) * mm, v(-27.63, -26.46) * mm, v(-27.57, -26.42) * mm, v(-26.8, -27.1) * mm, v(-26.77, -27.18) * mm, v(-27.55, -28.75) * mm, v(-27.52, -28.85) * mm, v(-26.46, -27.52) * mm, v(-26.31, -27.52) * mm, v(-25.77, -27.98) * mm, v(-25.9, -28.17) * mm, v(-28.5, -31.16) * mm, v(-28.55, -31.22) * mm, v(-29.31, -30.58) * mm, v(-29.3, -30.5) * mm, v(-28.38, -28.62) * mm, v(-28.39, -28.52) * mm, v(-29.7, -30.1) * mm, v(-29.78, -30.17) * mm]});
            skFitSpline(sketch, "E47", {"points": [v(-21.58, -32.95) * mm, v(-20.72, -31.56) * mm, v(-20.73, -31.51) * mm, v(-21.45, -31.08) * mm, v(-21.56, -31.05) * mm, v(-21.73, -31.33) * mm, v(-23.72, -34.66) * mm, v(-23.73, -34.72) * mm, v(-22.92, -35.2) * mm, v(-22.87, -35.15) * mm, v(-21.93, -33.52) * mm, v(-21.84, -33.48) * mm, v(-21.7, -33.53) * mm, v(-21.73, -33.7) * mm, v(-22.7, -35.27) * mm, v(-22.69, -35.34) * mm, v(-21.93, -35.77) * mm, v(-21.8, -35.71) * mm, v(-19.7, -32.16) * mm, v(-19.7, -32.12) * mm, v(-20.46, -31.64) * mm, v(-20.59, -31.68) * mm, v(-21.4, -33.1) * mm, v(-21.47, -33.06) * mm, v(-21.58, -32.95) * mm]});
            skFitSpline(sketch, "E48", {"points": [v(-25.43, -30.2) * mm, v(-24.75, -30.72) * mm, v(-24.5, -30.45) * mm, v(-24.1, -29.89) * mm, v(-24.24, -29.17) * mm, v(-25.04, -28.57) * mm, v(-25.73, -28.58) * mm, v(-26.08, -29.09) * mm, v(-27.74, -31.2) * mm, v(-27.67, -32.03) * mm, v(-27.06, -32.36) * mm, v(-26.74, -32.39) * mm, v(-26.8, -32.56) * mm, v(-26.37, -32.92) * mm, v(-26.27, -32.74) * mm, v(-25.12, -31.21) * mm, v(-25.06, -31.15) * mm, v(-25.88, -30.58) * mm, v(-25.89, -30.54) * mm, v(-26.14, -30.82) * mm, v(-26.36, -31.13) * mm, v(-26.27, -31.23) * mm, v(-26.76, -31.83) * mm, v(-26.92, -31.75) * mm, v(-26.8, -31.53) * mm, v(-25.14, -29.29) * mm, v(-25.05, -29.26) * mm, v(-24.92, -29.35) * mm, v(-24.91, -29.53) * mm, v(-25.34, -30.07) * mm, v(-25.43, -30.2) * mm]});
            skFitSpline(sketch, "E49", {"points": [v(-23.43, -30.5) * mm, v(-23.83, -30.22) * mm, v(-23.86, -30.2) * mm, v(-23.57, -29.75) * mm, v(-23.5, -29.7) * mm, v(-21.9, -30.8) * mm, v(-21.86, -30.84) * mm, v(-22.14, -31.29) * mm, v(-22.22, -31.31) * mm, v(-22.57, -31.06) * mm, v(-22.64, -31.02) * mm, v(-24.62, -34.02) * mm, v(-24.67, -34.08) * mm, v(-25.44, -33.57) * mm, v(-25.5, -33.5) * mm, v(-23.5, -30.63) * mm, v(-23.43, -30.5) * mm]});
            skFitSpline(sketch, "E50", {"points": [v(-14.84, -36.05) * mm, v(-14.12, -36.34) * mm, v(-14.05, -36.37) * mm, v(-13.7, -35.47) * mm, v(-13.8, -35) * mm, v(-14.36, -34.53) * mm, v(-15.28, -34.46) * mm, v(-15.63, -34.73) * mm, v(-16.74, -37.6) * mm, v(-16.71, -37.9) * mm, v(-16.68, -38.14) * mm, v(-16.02, -38.64) * mm, v(-15.24, -38.7) * mm, v(-14.77, -38.28) * mm, v(-14.4, -37.32) * mm, v(-14.38, -37.27) * mm, v(-15.15, -36.98) * mm, v(-15.25, -36.96) * mm, v(-15.6, -37.96) * mm, v(-15.73, -37.98) * mm, v(-15.82, -37.94) * mm, v(-14.76, -35.16) * mm, v(-14.72, -35.1) * mm, v(-14.6, -35.12) * mm, v(-14.57, -35.3) * mm, v(-14.8, -35.89) * mm, v(-14.84, -36.05) * mm]});
            skFitSpline(sketch, "E51", {"points": [v(-14.27, -38.6) * mm, v(-13.32, -35.64) * mm, v(-13.08, -35.35) * mm, v(-12.57, -35.26) * mm, v(-11.57, -35.59) * mm, v(-11.3, -36.07) * mm, v(-11.3, -36.39) * mm, v(-12.23, -39.34) * mm, v(-12.4, -39.42) * mm, v(-12.77, -39.57) * mm, v(-13.33, -39.5) * mm, v(-13.91, -39.28) * mm, v(-14.21, -38.91) * mm, v(-14.27, -38.6) * mm]});
            skFitSpline(sketch, "E52", {"points": [v(-12.45, -36) * mm, v(-12.33, -35.93) * mm, v(-12.17, -36) * mm, v(-12.18, -36.18) * mm, v(-13.06, -38.87) * mm, v(-13.08, -38.87) * mm, v(-13.23, -38.9) * mm, v(-13.33, -38.79) * mm, v(-13.3, -38.68) * mm, v(-12.45, -36) * mm]});
            skFitSpline(sketch, "E53", {"points": [v(-11.74, -39.95) * mm, v(-10.74, -35.82) * mm, v(-10.67, -35.77) * mm, v(-9.71, -36.07) * mm, v(-9.66, -36.17) * mm, v(-9.6, -37.98) * mm, v(-9.56, -37.91) * mm, v(-9.21, -36.27) * mm, v(-9.16, -36.17) * mm, v(-8.42, -36.35) * mm, v(-8.35, -36.37) * mm, v(-9.36, -40.42) * mm, v(-9.36, -40.5) * mm, v(-10.3, -40.31) * mm, v(-10.38, -40.28) * mm, v(-10.44, -38.27) * mm, v(-10.44, -38.07) * mm, v(-10.9, -40.01) * mm, v(-10.97, -40.13) * mm, v(-11.58, -40.01) * mm, v(-11.74, -39.95) * mm]});
            skFitSpline(sketch, "E54", {"points": [v(-8.72, -40.52) * mm, v(-8, -36.57) * mm, v(-7.97, -36.45) * mm, v(-6.56, -36.71) * mm, v(-6.02, -37.17) * mm, v(-6.08, -38.06) * mm, v(-6.5, -40.41) * mm, v(-7.1, -40.9) * mm, v(-8.6, -40.7) * mm, v(-8.72, -40.52) * mm]});
            skFitSpline(sketch, "E55", {"points": [v(-7.7, -40.18) * mm, v(-7.17, -37.26) * mm, v(-7.14, -37.17) * mm, v(-7, -37.26) * mm, v(-7.03, -37.81) * mm, v(-7.46, -40.18) * mm, v(-7.52, -40.23) * mm, v(-7.7, -40.18) * mm]});
            skFitSpline(sketch, "E56", {"points": [v(-5.41, -36.86) * mm, v(-4.6, -36.96) * mm, v(-4.52, -36.97) * mm, v(-4.57, -37.3) * mm, v(-5.04, -41.1) * mm, v(-5.1, -41.2) * mm, v(-5.95, -41.12) * mm, v(-6, -41.12) * mm, v(-5.5, -37.1) * mm, v(-5.41, -36.86) * mm]});
            skFitSpline(sketch, "E57", {"points": [v(-3.71, -37.63) * mm, v(-4.19, -37.61) * mm, v(-4.22, -37.58) * mm, v(-4.19, -37.1) * mm, v(-4.19, -37.02) * mm, v(-2.27, -37.15) * mm, v(-2.18, -37.2) * mm, v(-2.2, -37.67) * mm, v(-2.2, -37.75) * mm, v(-2.69, -37.7) * mm, v(-2.73, -37.72) * mm, v(-3, -41.3) * mm, v(-3.02, -41.38) * mm, v(-3.91, -41.32) * mm, v(-3.99, -41.3) * mm, v(-3.73, -37.83) * mm, v(-3.71, -37.63) * mm]});
            skFitSpline(sketch, "E58", {"points": [v(-1.77, -37.18) * mm, v(-0.9, -37.2) * mm, v(-0.84, -37.2) * mm, v(-0.95, -41.37) * mm, v(-0.95, -41.45) * mm, v(-1.89, -41.45) * mm, v(-1.94, -41.43) * mm, v(-1.8, -37.34) * mm, v(-1.77, -37.18) * mm]});
            skFitSpline(sketch, "E59", {"points": [v(-0.39, -41.07) * mm, v(-0.42, -37.89) * mm, v(-0.3, -37.49) * mm, v(0.14, -37.24) * mm, v(0.96, -37.19) * mm, v(1.6, -37.53) * mm, v(1.71, -38.29) * mm, v(1.78, -40.98) * mm, v(1.63, -41.21) * mm, v(1.28, -41.45) * mm, v(0.8, -41.52) * mm, v(0.12, -41.45) * mm, v(-0.24, -41.24) * mm, v(-0.39, -41.07) * mm]});
            skFitSpline(sketch, "E60", {"points": [v(0.52, -40.79) * mm, v(0.5, -38) * mm, v(0.53, -37.85) * mm, v(0.64, -37.8) * mm, v(0.75, -37.87) * mm, v(0.78, -38) * mm, v(0.83, -40.8) * mm, v(0.8, -40.9) * mm, v(0.68, -40.9) * mm, v(0.52, -40.79) * mm]});
            skFitSpline(sketch, "E61", {"points": [v(2.42, -41.45) * mm, v(2.09, -37.2) * mm, v(2.15, -37.19) * mm, v(3.06, -37.11) * mm, v(3.16, -37.12) * mm, v(3.73, -38.8) * mm, v(3.8, -38.88) * mm, v(3.66, -37.18) * mm, v(3.68, -37.02) * mm, v(4.45, -36.98) * mm, v(4.48, -37.03) * mm, v(4.78, -41.1) * mm, v(4.78, -41.21) * mm, v(4.69, -41.26) * mm, v(3.86, -41.34) * mm, v(3.8, -41.32) * mm, v(3.08, -39.44) * mm, v(3.03, -39.23) * mm, v(3.21, -41.37) * mm, v(3.17, -41.4) * mm, v(2.6, -41.47) * mm, v(2.42, -41.45) * mm]});
            skFitSpline(sketch, "E62", {"points": [v(5.42, -41.12) * mm, v(4.9, -37.03) * mm, v(4.88, -36.93) * mm, v(5.72, -36.8) * mm, v(5.84, -36.8) * mm, v(6.36, -40.95) * mm, v(6.4, -41.07) * mm, v(5.57, -41.15) * mm, v(5.42, -41.12) * mm]});
            skFitSpline(sketch, "E63", {"points": [v(7, -40.94) * mm, v(6.23, -36.84) * mm, v(6.21, -36.75) * mm, v(7.15, -36.62) * mm, v(7.24, -36.6) * mm, v(8.06, -38.26) * mm, v(8.1, -38.31) * mm, v(7.78, -36.6) * mm, v(7.8, -36.5) * mm, v(8.47, -36.37) * mm, v(8.56, -36.39) * mm, v(9.36, -40.48) * mm, v(9.37, -40.57) * mm, v(8.41, -40.7) * mm, v(8.34, -40.73) * mm, v(7.43, -38.78) * mm, v(7.38, -38.73) * mm, v(7.74, -40.73) * mm, v(7.73, -40.88) * mm, v(7.17, -40.95) * mm, v(7, -40.94) * mm]});
            skFitSpline(sketch, "E64", {"points": [v(10.47, -38.07) * mm, v(11.45, -37.86) * mm, v(11.52, -38.03) * mm, v(12.02, -39.9) * mm, v(12.01, -39.93) * mm, v(11.6, -40.02) * mm, v(11.52, -40) * mm, v(11.4, -39.84) * mm, v(11.25, -40.02) * mm, v(10.95, -40.2) * mm, v(10.47, -40.3) * mm, v(10.03, -40.13) * mm, v(9.84, -39.82) * mm, v(9.1, -36.9) * mm, v(9.15, -36.45) * mm, v(9.5, -36.11) * mm, v(10.26, -35.9) * mm, v(10.78, -35.97) * mm, v(11.13, -36.32) * mm, v(11.35, -37.24) * mm, v(11.36, -37.27) * mm, v(10.63, -37.45) * mm, v(10.46, -37.47) * mm, v(10.25, -36.68) * mm, v(10.15, -36.54) * mm, v(10.07, -36.58) * mm, v(10.06, -36.87) * mm, v(10.16, -37.18) * mm, v(10.46, -38.5) * mm, v(10.77, -39.54) * mm, v(10.86, -39.58) * mm, v(10.98, -39.48) * mm, v(10.87, -38.83) * mm, v(10.83, -38.68) * mm, v(10.61, -38.7) * mm, v(10.56, -38.6) * mm, v(10.48, -38.21) * mm, v(10.47, -38.07) * mm]});
            skFitSpline(sketch, "E65", {"points": [v(17.16, -35.13) * mm, v(17.89, -34.77) * mm, v(17.84, -34.45) * mm, v(17.44, -33.72) * mm, v(16.82, -33.62) * mm, v(15.97, -34) * mm, v(15.67, -34.43) * mm, v(15.83, -35.19) * mm, v(16.97, -37.67) * mm, v(17.25, -37.82) * mm, v(17.68, -37.9) * mm, v(18.45, -37.58) * mm, v(18.86, -37.1) * mm, v(18.9, -36.83) * mm, v(18.42, -35.76) * mm, v(18.37, -35.64) * mm, v(17.65, -35.95) * mm, v(17.56, -36.04) * mm, v(17.72, -36.38) * mm, v(18, -37) * mm, v(17.98, -37.12) * mm, v(17.84, -37.18) * mm, v(17.7, -36.87) * mm, v(16.6, -34.5) * mm, v(16.63, -34.36) * mm, v(16.76, -34.3) * mm, v(17.06, -34.98) * mm, v(17.16, -35.13) * mm]});
            skFitSpline(sketch, "E66", {"points": [v(19.44, -36.6) * mm, v(18, -33.77) * mm, v(17.98, -33.23) * mm, v(18.24, -32.92) * mm, v(19, -32.5) * mm, v(19.45, -32.47) * mm, v(19.9, -32.78) * mm, v(21.27, -35.42) * mm, v(21.36, -35.58) * mm, v(21.27, -35.98) * mm, v(20.7, -36.56) * mm, v(20.03, -36.75) * mm, v(19.57, -36.7) * mm, v(19.44, -36.6) * mm]});
            skFitSpline(sketch, "E67", {"points": [v(20.16, -35.98) * mm, v(18.85, -33.41) * mm, v(18.8, -33.3) * mm, v(18.94, -33.2) * mm, v(19.05, -33.26) * mm, v(20.37, -35.75) * mm, v(20.41, -35.9) * mm, v(20.34, -36) * mm, v(20.16, -35.98) * mm]});
            skFitSpline(sketch, "E68", {"points": [v(22.1, -35.63) * mm, v(20, -32.14) * mm, v(19.93, -32.02) * mm, v(20.89, -31.43) * mm, v(20.98, -31.39) * mm, v(22.35, -32.94) * mm, v(22.45, -33.01) * mm, v(21.69, -31.14) * mm, v(21.63, -30.97) * mm, v(22.62, -30.43) * mm, v(22.7, -30.34) * mm, v(24.92, -33.9) * mm, v(24.95, -33.99) * mm, v(24.33, -34.39) * mm, v(24.24, -34.48) * mm, v(23.15, -32.7) * mm, v(23.05, -32.54) * mm, v(23.86, -34.65) * mm, v(23.9, -34.74) * mm, v(23.4, -35.04) * mm, v(23.31, -35.1) * mm, v(21.83, -33.56) * mm, v(21.69, -33.44) * mm, v(22.76, -35.17) * mm, v(22.82, -35.29) * mm, v(22.32, -35.64) * mm, v(22.1, -35.63) * mm]});
            skFitSpline(sketch, "E69", {"points": [v(25.94, -27.87) * mm, v(26.53, -27.34) * mm, v(26.63, -27.28) * mm, v(28.94, -29.97) * mm, v(29.1, -30) * mm, v(29.2, -29.9) * mm, v(29.13, -29.7) * mm, v(26.95, -27.19) * mm, v(26.88, -27.07) * mm, v(27.47, -26.56) * mm, v(27.53, -26.52) * mm, v(30.04, -29.36) * mm, v(30.06, -29.74) * mm, v(29.85, -30.24) * mm, v(29.2, -30.73) * mm, v(28.5, -30.83) * mm, v(28.15, -30.56) * mm, v(26.08, -28.12) * mm, v(25.94, -27.87) * mm]});
            skFitSpline(sketch, "E70", {"points": [v(30.84, -29.17) * mm, v(27.83, -26.24) * mm, v(27.93, -26.16) * mm, v(28.55, -25.47) * mm, v(28.8, -25.55) * mm, v(30.14, -26.37) * mm, v(30.29, -26.43) * mm, v(29.05, -25.11) * mm, v(28.97, -25.05) * mm, v(29.45, -24.62) * mm, v(29.5, -24.54) * mm, v(32.42, -27.42) * mm, v(32.54, -27.59) * mm, v(31.9, -28.14) * mm, v(31.85, -28.24) * mm, v(30.1, -27.25) * mm, v(29.95, -27.15) * mm, v(31.3, -28.52) * mm, v(31.43, -28.68) * mm, v(31.03, -29.02) * mm, v(30.84, -29.17) * mm]});
            skFitSpline(sketch, "E71", {"points": [v(29.84, -24.22) * mm, v(30.34, -23.61) * mm, v(30.43, -23.5) * mm, v(33.54, -26.3) * mm, v(33.61, -26.39) * mm, v(33.03, -27.02) * mm, v(32.95, -27.06) * mm, v(29.94, -24.33) * mm, v(29.84, -24.22) * mm]});
            skFitSpline(sketch, "E72", {"points": [v(31.45, -23.17) * mm, v(31.18, -23.48) * mm, v(31.14, -23.54) * mm, v(30.76, -23.25) * mm, v(30.68, -23.17) * mm, v(31.9, -21.73) * mm, v(31.98, -21.67) * mm, v(32.38, -21.99) * mm, v(32.44, -22.05) * mm, v(32.12, -22.38) * mm, v(32.1, -22.44) * mm, v(34.87, -24.74) * mm, v(34.93, -24.82) * mm, v(34.41, -25.45) * mm, v(34.34, -25.53) * mm, v(31.53, -23.27) * mm, v(31.45, -23.17) * mm]});
            skFitSpline(sketch, "E73", {"points": [v(36.08, -23.32) * mm, v(36.6, -22.62) * mm, v(36.65, -22.54) * mm, v(35.21, -21.54) * mm, v(35.18, -21.45) * mm, v(33.7, -19.3) * mm, v(33.7, -19.3) * mm, v(33.25, -19.96) * mm, v(33.2, -20.04) * mm, v(34.03, -21.18) * mm, v(34.08, -21.29) * mm, v(32.8, -20.74) * mm, v(32.73, -20.72) * mm, v(32.2, -21.4) * mm, v(32.16, -21.48) * mm, v(34.72, -22.33) * mm, v(34.73, -22.34) * mm, v(35.9, -23.23) * mm, v(36.08, -23.32) * mm]});
            skCircle(sketch, "E74", {"center": v(-18.8, -35.65) * mm, "radius": 0.67 * mm});
            skCircle(sketch, "E75", {"center": v(14.08, -37.6) * mm, "radius": 0.64 * mm});
            skCircle(sketch, "E76", {"center": v(0.2, 2.3) * mm, "radius": 22.4 * mm});
            skPoint(sketch, "E76.first.point", {"position": v(-22.07, 0) * mm});
            skPoint(sketch, "E76.second.point", {"position": v(13.82, 20.07) * mm});
            skPoint(sketch, "E76.third.point", {"position": v(8.77, -18.4) * mm});
            skCircle(sketch, "E77", {"center": v(-0.09, 2.58) * mm, "radius": 38.12 * mm});
            skPoint(sketch, "E77.first.point", {"position": v(-37.36, -5.39) * mm});
            skPoint(sketch, "E77.second.point", {"position": v(27.44, 28.94) * mm});
            skPoint(sketch, "E77.third.point", {"position": v(6.45, -34.97) * mm});
            skCircle(sketch, "E78", {"center": v(-0.04, 2.52) * mm, "radius": 37.29 * mm});
            skPoint(sketch, "E78.first.point", {"position": v(-36.54, -5.09) * mm});
            skPoint(sketch, "E78.second.point", {"position": v(26.97, 28.23) * mm});
            skPoint(sketch, "E78.third.point", {"position": v(23.07, -26.74) * mm});
            skFitSpline(sketch, "E79", {"points": [v(23.05, -30.09) * mm, v(23.86, -29.48) * mm, v(23.96, -29.42) * mm, v(25.46, -30.72) * mm, v(25.57, -30.83) * mm, v(24.65, -29.03) * mm, v(24.63, -28.9) * mm, v(25.53, -28.2) * mm, v(25.62, -28.16) * mm, v(28.17, -31.53) * mm, v(28.2, -31.57) * mm, v(27.56, -32.1) * mm, v(27.48, -32.13) * mm, v(26.27, -30.46) * mm, v(26.15, -30.33) * mm, v(27.15, -32.36) * mm, v(27.15, -32.38) * mm, v(26.66, -32.76) * mm, v(26.55, -32.76) * mm, v(24.9, -31.34) * mm, v(24.76, -31.26) * mm, v(26.12, -32.98) * mm, v(26.17, -33.08) * mm, v(25.56, -33.56) * mm, v(25.53, -33.58) * mm, v(23.07, -30.26) * mm, v(23.05, -30.09) * mm]});
            skPoint(sketch, "E80.first.point", {"position": v(-22.17, 0) * mm});
            skPoint(sketch, "E80.second.point", {"position": v(14, 20.12) * mm});
            skPoint(sketch, "E80.third.point", {"position": v(8.77, -18.57) * mm});
            skSolve(sketch);
        }
        {
            var Q0;
            Q0=makeQuery(id+"F2.imprint","IMPRINT",FACE,{"disambiguationData":[TD([[makeQuery(id+"F2.imprint","IMPRINT",EDGE,{"derivedFrom":sQuery(id+"F2.wireOp",EDGE,"E1")}),1.0]])]});
            var Q1;
            Q1=makeQuery(id+"F2.imprint","IMPRINT",FACE,{"disambiguationData":[TD([[makeQuery(id+"F2.imprint","IMPRINT",EDGE,{"derivedFrom":sQuery(id+"F2.wireOp",EDGE,"E17")}),-1.0]])]});
            var Q2;
            Q2=makeQuery(id+"F2.imprint","IMPRINT",FACE,{"disambiguationData":[TD([[makeQuery(id+"F2.imprint","IMPRINT",EDGE,{"derivedFrom":sQuery(id+"F2.wireOp",EDGE,"E19")}),-1.0]])]});
            var Q3;
            Q3=makeQuery(id+"F2.imprint","IMPRINT",FACE,{"disambiguationData":[TD([[makeQuery(id+"F2.imprint","IMPRINT",EDGE,{"derivedFrom":sQuery(id+"F2.wireOp",EDGE,"E21")}),1.0]])]});
            var Q4;
            Q4=makeQuery(id+"F2.imprint","IMPRINT",FACE,{"disambiguationData":[TD([[makeQuery(id+"F2.imprint","IMPRINT",EDGE,{"derivedFrom":sQuery(id+"F2.wireOp",EDGE,"E22")}),-1.0]])]});
            var Q5;
            Q5=makeQuery(id+"F2.imprint","IMPRINT",FACE,{"disambiguationData":[TD([[makeQuery(id+"F2.imprint","IMPRINT",EDGE,{"derivedFrom":sQuery(id+"F2.wireOp",EDGE,"E23")}),-1.0]])]});
            var Q6;
            Q6=makeQuery(id+"F2.imprint","IMPRINT",FACE,{"disambiguationData":[TD([[makeQuery(id+"F2.imprint","IMPRINT",EDGE,{"derivedFrom":sQuery(id+"F2.wireOp",EDGE,"E24")}),-1.0]])]});
            var Q7;
            Q7=makeQuery(id+"F2.imprint","IMPRINT",FACE,{"disambiguationData":[TD([[makeQuery(id+"F2.imprint","IMPRINT",EDGE,{"derivedFrom":sQuery(id+"F2.wireOp",EDGE,"E25")}),-1.0]])]});
            var Q8;
            Q8=makeQuery(id+"F2.imprint","IMPRINT",FACE,{"disambiguationData":[TD([[makeQuery(id+"F2.imprint","IMPRINT",EDGE,{"derivedFrom":sQuery(id+"F2.wireOp",EDGE,"E26")}),1.0]])]});
            var Q9;
            Q9=makeQuery(id+"F2.imprint","IMPRINT",FACE,{"disambiguationData":[TD([[makeQuery(id+"F2.imprint","IMPRINT",EDGE,{"derivedFrom":sQuery(id+"F2.wireOp",EDGE,"E27")}),-1.0]])]});
            var Q10;
            Q10=makeQuery(id+"F2.imprint","IMPRINT",FACE,{"disambiguationData":[TD([[makeQuery(id+"F2.imprint","IMPRINT",EDGE,{"derivedFrom":sQuery(id+"F2.wireOp",EDGE,"E29")}),-1.0]])]});
            var Q11;
            Q11=makeQuery(id+"F2.imprint","IMPRINT",FACE,{"disambiguationData":[TD([[makeQuery(id+"F2.imprint","IMPRINT",EDGE,{"derivedFrom":sQuery(id+"F2.wireOp",EDGE,"E30")}),-1.0]])]});
            var Q12;
            Q12=makeQuery(id+"F2.imprint","IMPRINT",FACE,{"disambiguationData":[TD([[makeQuery(id+"F2.imprint","IMPRINT",EDGE,{"derivedFrom":sQuery(id+"F2.wireOp",EDGE,"E31")}),-1.0]])]});
            var Q13;
            Q13=makeQuery(id+"F2.imprint","IMPRINT",FACE,{"disambiguationData":[TD([[makeQuery(id+"F2.imprint","IMPRINT",EDGE,{"derivedFrom":sQuery(id+"F2.wireOp",EDGE,"E33")}),1.0]])]});
            var Q14;
            Q14=makeQuery(id+"F2.imprint","IMPRINT",FACE,{"disambiguationData":[TD([[makeQuery(id+"F2.imprint","IMPRINT",EDGE,{"derivedFrom":sQuery(id+"F2.wireOp",EDGE,"E34")}),-1.0]])]});
            var Q15;
            Q15=makeQuery(id+"F2.imprint","IMPRINT",FACE,{"disambiguationData":[TD([[makeQuery(id+"F2.imprint","IMPRINT",EDGE,{"derivedFrom":sQuery(id+"F2.wireOp",EDGE,"E8")}),-1.0]])]});
            var Q16;
            Q16=makeQuery(id+"F2.imprint","IMPRINT",FACE,{"disambiguationData":[TD([[makeQuery(id+"F2.imprint","IMPRINT",EDGE,{"derivedFrom":sQuery(id+"F2.wireOp",EDGE,"E39")}),-1.0]])]});
            var Q17;
            Q17=makeQuery(id+"F2.imprint","IMPRINT",FACE,{"disambiguationData":[TD([[makeQuery(id+"F2.imprint","IMPRINT",EDGE,{"derivedFrom":sQuery(id+"F2.wireOp",EDGE,"E40")}),-1.0]])]});
            var Q18;
            Q18=makeQuery(id+"F2.imprint","IMPRINT",FACE,{"disambiguationData":[TD([[makeQuery(id+"F2.imprint","IMPRINT",EDGE,{"derivedFrom":sQuery(id+"F2.wireOp",EDGE,"E38")}),1.0]])]});
            var Q19;
            Q19=makeQuery(id+"F2.imprint","IMPRINT",FACE,{"disambiguationData":[TD([[makeQuery(id+"F2.imprint","IMPRINT",EDGE,{"derivedFrom":sQuery(id+"F2.wireOp",EDGE,"E35")}),-1.0]])]});
            var Q20;
            Q20=makeQuery(id+"F2.imprint","IMPRINT",FACE,{"disambiguationData":[TD([[makeQuery(id+"F2.imprint","IMPRINT",EDGE,{"derivedFrom":sQuery(id+"F2.wireOp",EDGE,"E36")}),-1.0]])]});
            var Q21;
            Q21=makeQuery(id+"F2.imprint","IMPRINT",FACE,{"disambiguationData":[TD([[makeQuery(id+"F2.imprint","IMPRINT",EDGE,{"derivedFrom":sQuery(id+"F2.wireOp",EDGE,"E41")}),1.0]])]});
            var Q22;
            Q22=makeQuery(id+"F2.imprint","IMPRINT",FACE,{"disambiguationData":[TD([[makeQuery(id+"F2.imprint","IMPRINT",EDGE,{"derivedFrom":sQuery(id+"F2.wireOp",EDGE,"E42")}),-1.0]])]});
            var Q23;
            Q23=makeQuery(id+"F2.imprint","IMPRINT",FACE,{"disambiguationData":[TD([[makeQuery(id+"F2.imprint","IMPRINT",EDGE,{"derivedFrom":sQuery(id+"F2.wireOp",EDGE,"E43")}),-1.0]])]});
            var Q24;
            Q24=makeQuery(id+"F2.imprint","IMPRINT",FACE,{"disambiguationData":[TD([[makeQuery(id+"F2.imprint","IMPRINT",EDGE,{"derivedFrom":sQuery(id+"F2.wireOp",EDGE,"E45")}),1.0]])]});
            var Q25;
            Q25=makeQuery(id+"F2.imprint","IMPRINT",FACE,{"disambiguationData":[TD([[makeQuery(id+"F2.imprint","IMPRINT",EDGE,{"derivedFrom":sQuery(id+"F2.wireOp",EDGE,"E46")}),-1.0]])]});
            var Q26;
            Q26=makeQuery(id+"F2.imprint","IMPRINT",FACE,{"disambiguationData":[TD([[makeQuery(id+"F2.imprint","IMPRINT",EDGE,{"derivedFrom":sQuery(id+"F2.wireOp",EDGE,"E49")}),-1.0]])]});
            var Q27;
            Q27=makeQuery(id+"F2.imprint","IMPRINT",FACE,{"disambiguationData":[TD([[makeQuery(id+"F2.imprint","IMPRINT",EDGE,{"derivedFrom":sQuery(id+"F2.wireOp",EDGE,"E48")}),1.0]])]});
            var Q28;
            Q28=makeQuery(id+"F2.imprint","IMPRINT",FACE,{"disambiguationData":[TD([[makeQuery(id+"F2.imprint","IMPRINT",EDGE,{"derivedFrom":sQuery(id+"F2.wireOp",EDGE,"E47")}),1.0]])]});
            var Q29;
            Q29=makeQuery(id+"F2.imprint","IMPRINT",FACE,{"disambiguationData":[TD([[makeQuery(id+"F2.imprint","IMPRINT",EDGE,{"derivedFrom":sQuery(id+"F2.wireOp",EDGE,"E74")}),1.0]])]});
            var Q30;
            Q30=makeQuery(id+"F2.imprint","IMPRINT",FACE,{"disambiguationData":[TD([[makeQuery(id+"F2.imprint","IMPRINT",EDGE,{"derivedFrom":sQuery(id+"F2.wireOp",EDGE,"E50")}),1.0]])]});
            var Q31;
            Q31=makeQuery(id+"F2.imprint","IMPRINT",FACE,{"disambiguationData":[TD([[makeQuery(id+"F2.imprint","IMPRINT",EDGE,{"derivedFrom":sQuery(id+"F2.wireOp",EDGE,"E51")}),-1.0]])]});
            var Q32;
            Q32=makeQuery(id+"F2.imprint","IMPRINT",FACE,{"disambiguationData":[TD([[makeQuery(id+"F2.imprint","IMPRINT",EDGE,{"derivedFrom":sQuery(id+"F2.wireOp",EDGE,"E53")}),-1.0]])]});
            var Q33;
            Q33=makeQuery(id+"F2.imprint","IMPRINT",FACE,{"disambiguationData":[TD([[makeQuery(id+"F2.imprint","IMPRINT",EDGE,{"derivedFrom":sQuery(id+"F2.wireOp",EDGE,"E54")}),-1.0]])]});
            var Q34;
            Q34=makeQuery(id+"F2.imprint","IMPRINT",FACE,{"disambiguationData":[TD([[makeQuery(id+"F2.imprint","IMPRINT",EDGE,{"derivedFrom":sQuery(id+"F2.wireOp",EDGE,"E56")}),-1.0]])]});
            var Q35;
            Q35=makeQuery(id+"F2.imprint","IMPRINT",FACE,{"disambiguationData":[TD([[makeQuery(id+"F2.imprint","IMPRINT",EDGE,{"derivedFrom":sQuery(id+"F2.wireOp",EDGE,"E57")}),-1.0]])]});
            var Q36;
            Q36=makeQuery(id+"F2.imprint","IMPRINT",FACE,{"disambiguationData":[TD([[makeQuery(id+"F2.imprint","IMPRINT",EDGE,{"derivedFrom":sQuery(id+"F2.wireOp",EDGE,"E58")}),-1.0]])]});
            var Q37;
            Q37=makeQuery(id+"F2.imprint","IMPRINT",FACE,{"disambiguationData":[TD([[makeQuery(id+"F2.imprint","IMPRINT",EDGE,{"derivedFrom":sQuery(id+"F2.wireOp",EDGE,"E59")}),-1.0]])]});
            var Q38;
            Q38=makeQuery(id+"F2.imprint","IMPRINT",FACE,{"disambiguationData":[TD([[makeQuery(id+"F2.imprint","IMPRINT",EDGE,{"derivedFrom":sQuery(id+"F2.wireOp",EDGE,"E61")}),-1.0]])]});
            var Q39;
            Q39=makeQuery(id+"F2.imprint","IMPRINT",FACE,{"disambiguationData":[TD([[makeQuery(id+"F2.imprint","IMPRINT",EDGE,{"derivedFrom":sQuery(id+"F2.wireOp",EDGE,"E63")}),-1.0]])]});
            var Q40;
            Q40=makeQuery(id+"F2.imprint","IMPRINT",FACE,{"disambiguationData":[TD([[makeQuery(id+"F2.imprint","IMPRINT",EDGE,{"derivedFrom":sQuery(id+"F2.wireOp",EDGE,"E64")}),-1.0]])]});
            var Q41;
            Q41=makeQuery(id+"F2.imprint","IMPRINT",FACE,{"disambiguationData":[TD([[makeQuery(id+"F2.imprint","IMPRINT",EDGE,{"derivedFrom":sQuery(id+"F2.wireOp",EDGE,"E75")}),1.0]])]});
            var Q42;
            Q42=makeQuery(id+"F2.imprint","IMPRINT",FACE,{"disambiguationData":[TD([[makeQuery(id+"F2.imprint","IMPRINT",EDGE,{"derivedFrom":sQuery(id+"F2.wireOp",EDGE,"E62")}),-1.0]])]});
            var Q43;
            Q43=makeQuery(id+"F2.imprint","IMPRINT",FACE,{"disambiguationData":[TD([[makeQuery(id+"F2.imprint","IMPRINT",EDGE,{"derivedFrom":sQuery(id+"F2.wireOp",EDGE,"E37")}),1.0]])]});
            var Q44;
            Q44=makeQuery(id+"F2.imprint","IMPRINT",FACE,{"disambiguationData":[TD([[makeQuery(id+"F2.imprint","IMPRINT",EDGE,{"derivedFrom":sQuery(id+"F2.wireOp",EDGE,"E65")}),1.0]])]});
            var Q45;
            Q45=makeQuery(id+"F2.imprint","IMPRINT",FACE,{"disambiguationData":[TD([[makeQuery(id+"F2.imprint","IMPRINT",EDGE,{"derivedFrom":sQuery(id+"F2.wireOp",EDGE,"E66")}),-1.0]])]});
            var Q46;
            Q46=makeQuery(id+"F2.imprint","IMPRINT",FACE,{"disambiguationData":[TD([[makeQuery(id+"F2.imprint","IMPRINT",EDGE,{"derivedFrom":sQuery(id+"F2.wireOp",EDGE,"E68")}),-1.0]])]});
            var Q47;
            Q47=makeQuery(id+"F2.imprint","IMPRINT",FACE,{"disambiguationData":[TD([[makeQuery(id+"F2.imprint","IMPRINT",EDGE,{"derivedFrom":sQuery(id+"F2.wireOp",EDGE,"E73")}),1.0]])]});
            var Q48;
            Q48=makeQuery(id+"F2.imprint","IMPRINT",FACE,{"disambiguationData":[TD([[makeQuery(id+"F2.imprint","IMPRINT",EDGE,{"derivedFrom":sQuery(id+"F2.wireOp",EDGE,"E72")}),-1.0]])]});
            var Q49;
            Q49=makeQuery(id+"F2.imprint","IMPRINT",FACE,{"disambiguationData":[TD([[makeQuery(id+"F2.imprint","IMPRINT",EDGE,{"derivedFrom":sQuery(id+"F2.wireOp",EDGE,"E71")}),-1.0]])]});
            var Q50;
            Q50=makeQuery(id+"F2.imprint","IMPRINT",FACE,{"disambiguationData":[TD([[makeQuery(id+"F2.imprint","IMPRINT",EDGE,{"derivedFrom":sQuery(id+"F2.wireOp",EDGE,"E70")}),-1.0]])]});
            var Q51;
            Q51=makeQuery(id+"F2.imprint","IMPRINT",FACE,{"disambiguationData":[TD([[makeQuery(id+"F2.imprint","IMPRINT",EDGE,{"derivedFrom":sQuery(id+"F2.wireOp",EDGE,"E69")}),-1.0]])]});
            var Q52;
            Q52=makeQuery(id+"F2.imprint","IMPRINT",FACE,{"disambiguationData":[TD([[makeQuery(id+"F2.imprint","IMPRINT",EDGE,{"derivedFrom":sQuery(id+"F2.wireOp",EDGE,"E79")}),-1.0]])]});
            var Q53;
            Q53=makeQuery(id+"F2.imprint","IMPRINT",FACE,{"disambiguationData":[TD([[makeQuery(id+"F2.imprint","IMPRINT",EDGE,{"derivedFrom":sQuery(id+"F2.wireOp",EDGE,"E77")}),1.0]])]});
            extrude(context, id + "F3", {"entities" : qUnion([Q0, Q1, Q2, Q3, Q4, Q5, Q6, Q7, Q8, Q9, Q10, Q11, Q12, Q13, Q14, Q15, Q16, Q17, Q18, Q19, Q20, Q21, Q22, Q23, Q24, Q25, Q26, Q27, Q28, Q29, Q30, Q31, Q32, Q33, Q34, Q35, Q36, Q37, Q38, Q39, Q40, Q41, Q42, Q43, Q44, Q45, Q46, Q47, Q48, Q49, Q50, Q51, Q52, Q53]), "operationType" : NewBodyOperationType.ADD, "depth" : 2.03 * mm});
        }
        {
            var Q0;
            {var subQ0=sQuery(id+"F0.wireOp",EDGE,"E0");Q0=makeQuery(id+"F3.boolean.opBoolean","SPLIT",FACE,{"disambiguationData":[TD([makeQuery(id+"F1.opExtrude","SWEPT_FACE",FACE,{"disambiguationData":[OSD([subQ0])]})])],"derivedFrom":makeQuery(id+"F1.opExtrude","CAP_FACE",FACE,{"disambiguationData":[OSD([subQ0])],"isStart":false})});}
            var sketch = newSketch(context, id + "F4", { "sketchPlane" : qUnion([Q0])});
            skLineSegment(sketch, "E81", {"start": v(-63.5, -57.15) * mm, "end": v(63.5, -57.15) * mm});
            skLineSegment(sketch, "E82", {"start": v(-63.5, -57.15) * mm, "end": v(-63.5, -60.33) * mm});
            skLineSegment(sketch, "E83", {"start": v(-63.5, -60.33) * mm, "end": v(63.5, -60.33) * mm});
            skLineSegment(sketch, "E84", {"start": v(63.5, -60.33) * mm, "end": v(63.5, -57.15) * mm});
            skSolve(sketch);
        }
        {
            var Q0;
            {var subQ0=sQuery(id+"F4.wireOp",EDGE,"E82");Q0=makeQuery(id+"F4.imprint","IMPRINT",FACE,{"disambiguationData":[TD([[makeQuery(id+"F4.imprint","IMPRINT",EDGE,{"derivedFrom":subQ0}),1.0]])]});}
            extrude(context, id + "F5", {"entities" : qUnion([Q0]), "oppositeDirection" : true, "depth" : 12.7 * mm});
        }
        {
            var Q0;
            Q0=makeQuery(id+"F5.opExtrude","CAP_FACE",FACE,{"disambiguationData":[OSD([sQuery(id+"F4.wireOp",EDGE,"E81"),sQuery(id+"F4.wireOp",EDGE,"E82"),sQuery(id+"F4.wireOp",EDGE,"E83"),sQuery(id+"F4.wireOp",EDGE,"E84")])],"isStart":true});
            var sketch = newSketch(context, id + "F6", { "sketchPlane" : qUnion([Q0])});
            skLineSegment(sketch, "E85.0", {"start": v(-63.5, -57.15) * mm, "end": v(63.5, -57.15) * mm});
            skCircle(sketch, "E86.0", {"center": v(0, 0) * mm, "radius": 57.15 * mm});
            skArc(sketch, "E87", {"start": v(-45.14, -57.15) * mm, "mid": v(-37.64, -53.25) * mm, "end": v(-34.92, -45.24) * mm});
            skSolve(sketch);
        }
        {
            var Q0;
            {var subQ0=sQuery(id+"F6.wireOp",EDGE,"E87");Q0=makeQuery(id+"F6.imprint","IMPRINT",FACE,{"disambiguationData":[TD([[makeQuery(id+"F6.imprint","IMPRINT",EDGE,{"derivedFrom":subQ0}),-1.0]])]});}
            extrude(context, id + "F7", {"entities" : qUnion([Q0]), "oppositeDirection" : true, "depth" : 12.7 * mm});
        }
        {
            var Q0;
            Q0=makeQuery(id+"F7.opExtrude","SWEPT_BODY",BODY,{"disambiguationData":[OSD([sQuery(id+"F6.wireOp",EDGE,"E85.0"),sQuery(id+"F6.wireOp",EDGE,"E86.0"),sQuery(id+"F6.wireOp",EDGE,"E87")])]});
            var Q1;
            Q1=qCreatedBy(makeId("Right.planeOp"),FACE);
            mirror(context, id + "F8", {"entities" : qUnion([Q0]), "mirrorPlane" : qUnion([Q1])});
        }
        {
            var Q0;
            Q0=makeQuery(id+"F1.opExtrude","SWEPT_BODY",BODY,{"disambiguationData":[OSD([sQuery(id+"F0.wireOp",EDGE,"E0")])]});
            var Q1;
            Q1=makeQuery(id+"F5.opExtrude","SWEPT_BODY",BODY,{"disambiguationData":[OSD([sQuery(id+"F4.wireOp",EDGE,"E81"),sQuery(id+"F4.wireOp",EDGE,"E82"),sQuery(id+"F4.wireOp",EDGE,"E83"),sQuery(id+"F4.wireOp",EDGE,"E84")])]});
            var Q2;
            Q2=makeQuery(id+"F7.opExtrude","SWEPT_BODY",BODY,{"disambiguationData":[OSD([sQuery(id+"F6.wireOp",EDGE,"E85.0"),sQuery(id+"F6.wireOp",EDGE,"E86.0"),sQuery(id+"F6.wireOp",EDGE,"E87")])]});
            var Q3;
            Q3=makeQuery(id+"F8.opPattern","COPY",BODY,{"derivedFrom":makeQuery(id+"F7.opExtrude","SWEPT_BODY",BODY,{"disambiguationData":[OSD([sQuery(id+"F6.wireOp",EDGE,"E85.0"),sQuery(id+"F6.wireOp",EDGE,"E86.0"),sQuery(id+"F6.wireOp",EDGE,"E87")])]}),"instanceName":"1"});
            booleanBodies(context, id + "F9", {"operationType" : BooleanOperationType.UNION, "tools" : qUnion([Q0, Q1, Q2, Q3])});
        }
        {
            var Q0;
            {var subQ0=makeQuery(id+"F7.opExtrude","CAP_FACE",FACE,{"disambiguationData":[OSD([sQuery(id+"F6.wireOp",EDGE,"E85.0"),sQuery(id+"F6.wireOp",EDGE,"E86.0"),sQuery(id+"F6.wireOp",EDGE,"E87")])],"isStart":true});var subQ1=sQuery(id+"F0.wireOp",EDGE,"E0");Q0=makeQuery(id+"F9.opBoolean","MERGE",FACE,{"derivedFrom":[makeQuery(id+"F3.boolean.opBoolean","SPLIT",FACE,{"disambiguationData":[TD([makeQuery(id+"F1.opExtrude","SWEPT_FACE",FACE,{"disambiguationData":[OSD([subQ1])]})])],"derivedFrom":makeQuery(id+"F1.opExtrude","CAP_FACE",FACE,{"disambiguationData":[OSD([subQ1])],"isStart":false})}),makeQuery(id+"F5.opExtrude","CAP_FACE",FACE,{"disambiguationData":[OSD([sQuery(id+"F4.wireOp",EDGE,"E81"),sQuery(id+"F4.wireOp",EDGE,"E82"),sQuery(id+"F4.wireOp",EDGE,"E83"),sQuery(id+"F4.wireOp",EDGE,"E84")])],"isStart":true}),subQ0,makeQuery(id+"F8.opPattern","COPY",FACE,{"derivedFrom":subQ0,"instanceName":"1"})]});}
            var sketch = newSketch(context, id + "F10", { "sketchPlane" : qUnion([Q0])});
            skLineSegment(sketch, "E88.bottom", {"start": v(-63.5, -57.15) * mm, "end": v(63.5, -57.15) * mm});
            skLineSegment(sketch, "E88.top", {"start": v(-63.5, -60.33) * mm, "end": v(63.5, -60.33) * mm});
            skLineSegment(sketch, "E88.left", {"start": v(-63.5, -57.15) * mm, "end": v(-63.5, -60.33) * mm});
            skLineSegment(sketch, "E88.right", {"start": v(63.5, -57.15) * mm, "end": v(63.5, -60.33) * mm});
            skSolve(sketch);
        }
        {
            var Q0;
            Q0=makeQuery(id+"F10.imprint","IMPRINT",FACE,{"disambiguationData":[TD([[makeQuery(id+"F10.imprint","IMPRINT",EDGE,{"derivedFrom":sQuery(id+"F10.wireOp",EDGE,"E88.top")}),1.0]])]});
            extrude(context, id + "F11", {"entities" : qUnion([Q0]), "operationType" : NewBodyOperationType.ADD, "depth" : 12.7 * mm});
        }
    });
